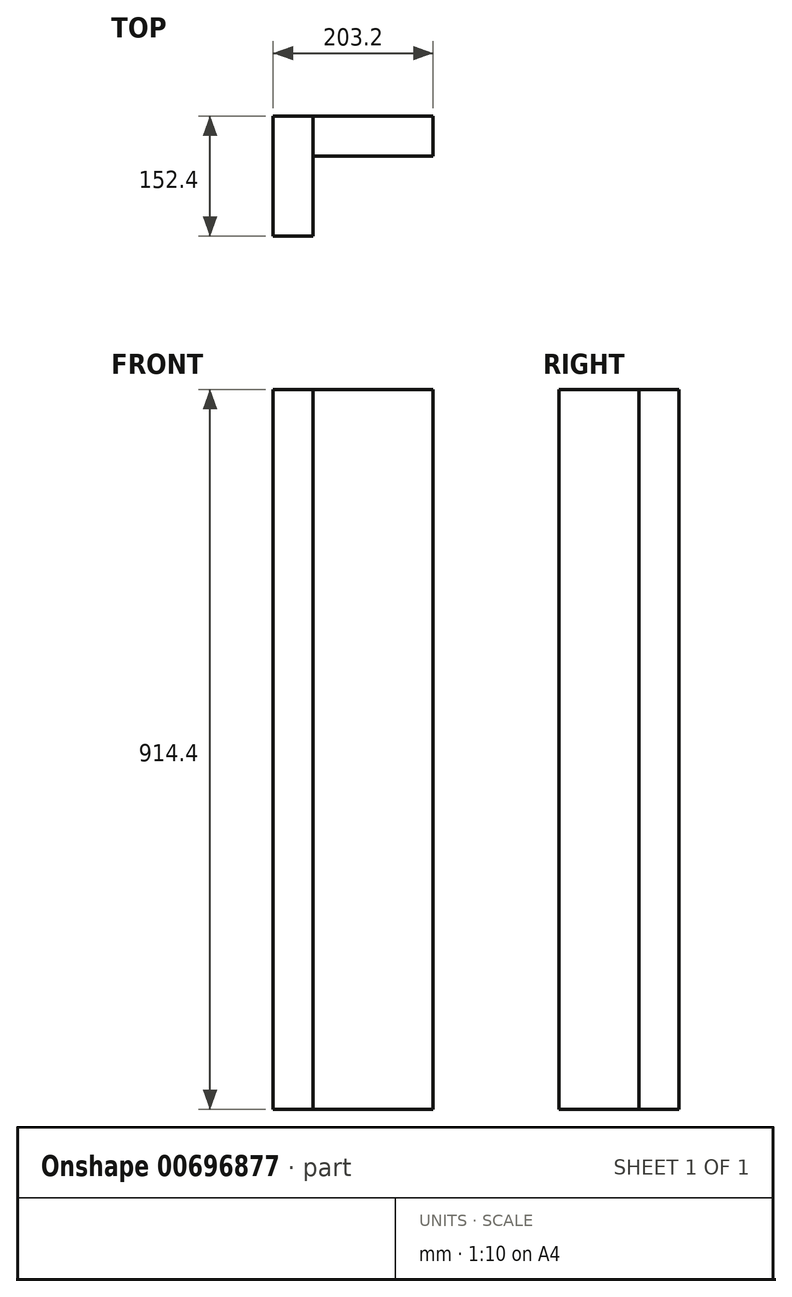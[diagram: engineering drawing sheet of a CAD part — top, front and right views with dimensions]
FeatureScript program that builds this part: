
annotation { "Feature Type Name" : "Feature", "Feature Type Description" : "" }
export const myFeature = defineFeature(function(context is Context, id is Id, definition is map)
    precondition{}
    {
        {
            var Q0;
            Q0=qCreatedBy(makeId("Top.planeOp"),FACE);
            var sketch = newSketch(context, id + "F0", { "sketchPlane" : qUnion([Q0])});
            skLineSegment(sketch, "E0.bottom", {"start": v(0, 0) * mm, "end": v(-50.8, 0) * mm});
            skLineSegment(sketch, "E0.top", {"start": v(0, -152.4) * mm, "end": v(-50.8, -152.4) * mm});
            skLineSegment(sketch, "E0.left", {"start": v(0, 0) * mm, "end": v(0, -152.4) * mm});
            skLineSegment(sketch, "E0.right", {"start": v(-50.8, 0) * mm, "end": v(-50.8, -152.4) * mm});
            skLineSegment(sketch, "E1.bottom", {"start": v(0, 0) * mm, "end": v(152.4, 0) * mm});
            skLineSegment(sketch, "E1.top", {"start": v(0, -50.8) * mm, "end": v(152.4, -50.8) * mm});
            skLineSegment(sketch, "E1.left", {"start": v(0, 0) * mm, "end": v(0, -50.8) * mm});
            skLineSegment(sketch, "E1.right", {"start": v(152.4, 0) * mm, "end": v(152.4, -50.8) * mm});
            skSolve(sketch);
        }
        {
            var Q0;
            Q0=makeQuery(id+"F0.imprint","IMPRINT",FACE,{"disambiguationData":[TD([[makeQuery(id+"F0.imprint","IMPRINT",EDGE,{"derivedFrom":sQuery(id+"F0.wireOp",EDGE,"E1.bottom")}),-1.0]])]});
            extrude(context, id + "F1", {"entities" : qUnion([Q0]), "oppositeDirection" : true, "depth" : 914.4 * mm, "offsetDistance" : 25.4 * mm});
        }
        {
            var Q0;
            Q0=makeQuery(id+"F0.imprint","IMPRINT",FACE,{"disambiguationData":[TD([[makeQuery(id+"F0.imprint","IMPRINT",EDGE,{"derivedFrom":sQuery(id+"F0.wireOp",EDGE,"E0.bottom")}),1.0]])]});
            extrude(context, id + "F2", {"entities" : qUnion([Q0]), "oppositeDirection" : true, "depth" : 914.4 * mm, "offsetDistance" : 25.4 * mm});
        }
    });
